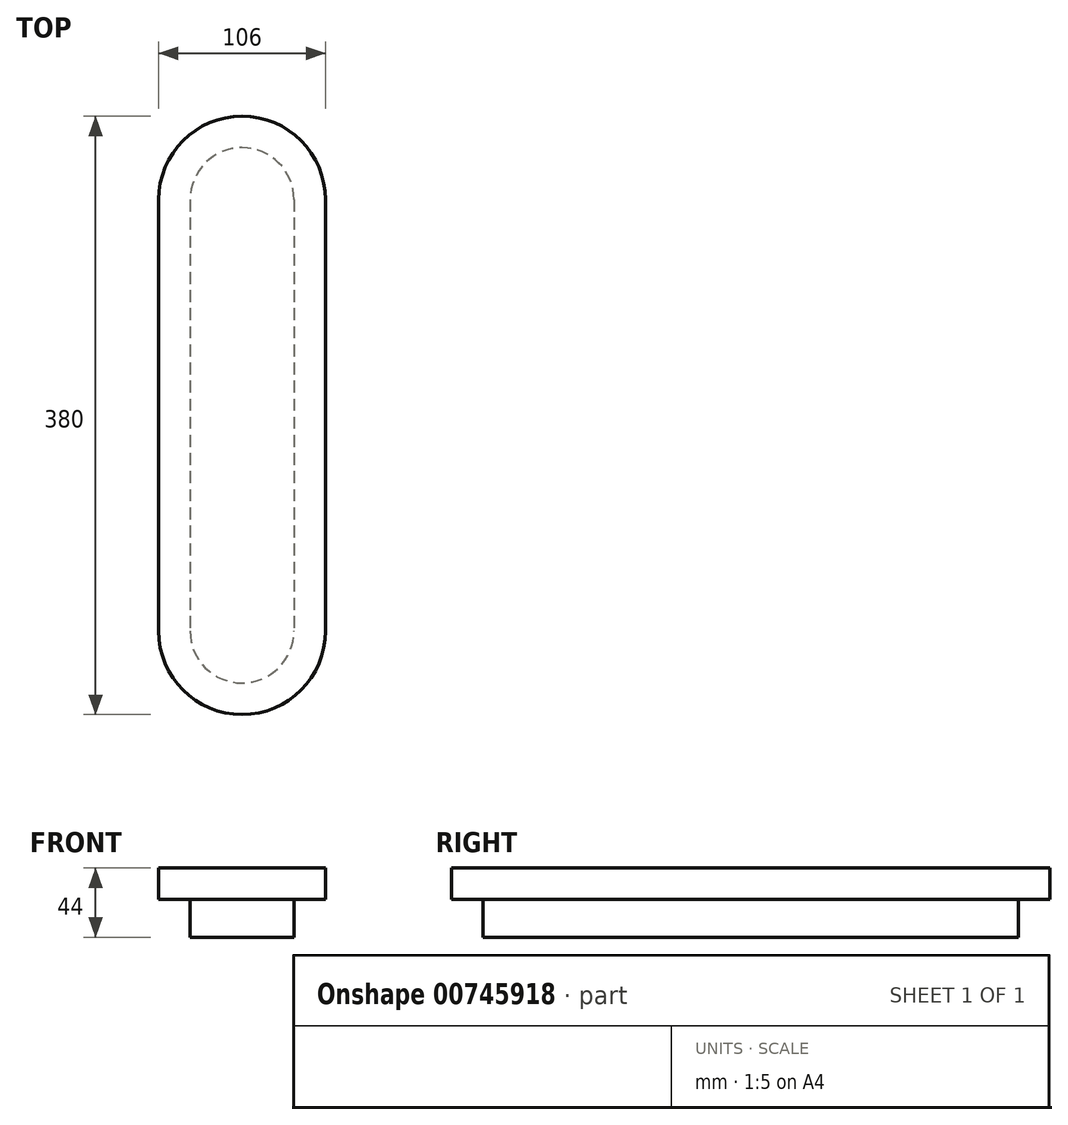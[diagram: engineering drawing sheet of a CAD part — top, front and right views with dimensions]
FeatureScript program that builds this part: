
annotation { "Feature Type Name" : "Feature", "Feature Type Description" : "" }
export const myFeature = defineFeature(function(context is Context, id is Id, definition is map)
    precondition{}
    {
        {
            var Q0;
            Q0=qCreatedBy(makeId("Top.planeOp"),FACE);
            var sketch = newSketch(context, id + "F0", { "sketchPlane" : qUnion([Q0])});
            skLineSegment(sketch, "E0.left", {"start": v(-33, 137) * mm, "end": v(-33, -137) * mm});
            skLineSegment(sketch, "E0.right", {"start": v(33, 137) * mm, "end": v(33, -137) * mm});
            skPoint(sketch, "E0.middle", {"position": v(0, 0) * mm});
            skLineSegment(sketch, "E1.left", {"start": v(53, -137) * mm, "end": v(53, 137) * mm});
            skLineSegment(sketch, "E1.right", {"start": v(-53, -137) * mm, "end": v(-53, 137) * mm});
            skLineSegment(sketch, "E2", {"start": v(0, -170) * mm, "end": v(0, 178.42) * mm, "construction": true});
            skArc(sketch, "E3", {"start": v(33, 137) * mm, "mid": v(0, 170) * mm, "end": v(-33, 137) * mm});
            skArc(sketch, "E4", {"start": v(-33, -137) * mm, "mid": v(0, -170) * mm, "end": v(33, -137) * mm});
            skArc(sketch, "E5", {"start": v(53, 137) * mm, "mid": v(0, 190) * mm, "end": v(-53, 137) * mm});
            skArc(sketch, "E6", {"start": v(-53, -137) * mm, "mid": v(0, -190) * mm, "end": v(53, -137) * mm});
            skLineSegment(sketch, "E7", {"start": v(-53, 137) * mm, "end": v(53, 137) * mm, "construction": true});
            skLineSegment(sketch, "E8", {"start": v(-53, -137) * mm, "end": v(53, -137) * mm, "construction": true});
            skSolve(sketch);
        }
        {
            var Q0;
            Q0=makeQuery(id+"F0.imprint","IMPRINT",FACE,{"disambiguationData":[TD([[makeQuery(id+"F0.imprint","IMPRINT",EDGE,{"derivedFrom":sQuery(id+"F0.wireOp",EDGE,"E0.left")}),1.0]])]});
            extrude(context, id + "F1", {"entities" : qUnion([Q0]), "oppositeDirection" : true, "depth" : 44 * mm, "offsetDistance" : 25 * mm});
        }
        {
            var Q0;
            Q0=makeQuery(id+"F0.imprint","IMPRINT",FACE,{"disambiguationData":[TD([[makeQuery(id+"F0.imprint","IMPRINT",EDGE,{"derivedFrom":sQuery(id+"F0.wireOp",EDGE,"E0.left")}),-1.0]])]});
            extrude(context, id + "F2", {"entities" : qUnion([Q0]), "operationType" : NewBodyOperationType.ADD, "oppositeDirection" : true, "depth" : 20 * mm, "offsetDistance" : 25 * mm});
        }
    });
